# Revit family: Legrand Emergency Lighting_BAP-SPOTLIGHT
name_source: partatom
category: Luminaires
units: mm (PartAtom-declared; Revit-internal decimal feet)

## family parameters
Cote de connecteur circulaire = Utiliser le diamètre
Couper avec des vides une fois chargée = Non
Hôte = Face
Partagée = Non
Repere pour localisation dans la piece = Non
Source d'éclairage = Non
Type d'élément = Normal

## types (8) — shared parameters
Color = Black
Connected Object = Non
Connection type = other
ETIM Class = EC001957-Emergency luminaire
Elévation par défaut = 2300 mm
Emergency power supply = Autonomous (individual battery)
Fabricant = Legrand
Frequency = 50/60 Hz
Function = Escape and mood lighting
General Conditions of Use = https://export.legrand.com
Height = 94 mm
IK = 07
IP = 65
Installation method = Surface mounting (wall)
Material = Plastic
Operating temperature MIN-MAX = 0°C +35°C
Pictogram type = other
Power supply = 230 VAC
Protection class = II
Standby consumption = 0 A
Switching type = Non permanent
System power = 1 W
URL = https://www.legrand.fr
battery status = Lithium-ion
light source = LED not exchangeable
terminal capacity = 1,5-2,5 mm2

## per-type parameters (varying)
| type | 1 phare 1000lm | 2 phares 1500lm | 2 phares 2500lm | Autonomy | Control system | EAN Code | Large | Length | Long | Product Description | Reference | Spare battery | Useful luminous flux | Width |
| Spotlight Autotest 2500 lm 1H | Non | Non | Oui | 1 H | Autotest Automatic | 3414972656030 | 240 mm  [stored 0.787402 ft] | 286 mm | 286 mm | TWIN LEDS SPOTLIGHT EMERGENCY LIGHTING UNIT NON MAINTAINED 2500LM 1H AUTOTEST | 660463 | 2 x 660977 | 2500 lm | 240 mm  [stored 0.787402 ft] |
| Spotlight Autotest 1000 lm 1H | Oui | Non | Non | 1 H | Autotest Automatic | 3414972656016 | 137 mm  [stored 0.449475 ft] | 409 mm | 409 mm | SPOTLIGHT EMERGENCY LIGHTING UNIT NON MAINTAINED 1000LM 1H AUTOTEST | 660460 | 660976 | 1000 lm | 137 mm  [stored 0.449475 ft] |
| Spotlight Autotest 1500 lm 1H | Non | Oui | Non | 1 H | Autotest Automatic | 3414972656023 | 240 mm  [stored 0.787402 ft] | 286 mm | 286 mm | TWIN LEDS SPOTLIGHT EMERGENCY LIGHTING UNIT NON MAINTAINED 1500LM 1H AUTOTEST | 660462 | 1 x 660977 | 1500 lm | 240 mm  [stored 0.787402 ft] |
| Spotlight Autotest 1500 lm 2H | Non | Oui | Non | 2 H | Autotest Automatic | 3414972656047 | 240 mm  [stored 0.787402 ft] | 286 mm | 286 mm | TWIN LEDS SPOTLIGHT EMERGENCY LIGHTING UNIT NON MAINTAINED 1500LM 2H AUTOTEST | 660465 | 2 x 660977 | 1500 lm | 240 mm  [stored 0.787402 ft] |
| Spotlight Standard 1000 lm 1H | Oui | Non | Non | 1 H | Control key | 3414972656054 | 137 mm  [stored 0.449475 ft] | 409 mm | 409 mm | SPOTLIGHT EMERGENCY LIGHTING UNIT NON MAINTAINED 1000LM 1H STANDARD | 661460 | 660976 | 1000 lm | 137 mm  [stored 0.449475 ft] |
| Spotlight Standard 1500 lm 1H | Non | Oui | Non | 1 H | Control key | 3414972656061 | 240 mm  [stored 0.787402 ft] | 286 mm | 286 mm | TWIN LEDS SPOTLIGHT EMERGENCY LIGHTING UNIT NON MAINTAINED 1500LM 1H STANDARD | 661462 | 660977 | 1500 lm | 240 mm  [stored 0.787402 ft] |
| Spotlight Standard 2500 lm 1H | Non | Non | Oui | 1 H | Control key | 3414972656078 | 240 mm  [stored 0.787402 ft] | 286 mm | 286 mm | TWIN LEDS SPOTLIGHT EMERGENCY LIGHTING UNIT NON MAINTAINED 2500LM 1H STANDARD | 661463 | 2 x 660977 | 2500 lm | 240 mm  [stored 0.787402 ft] |
| Spotlight Adressable 2500 lm 1H | Non | Non | Oui | 1 H | Autotest Automatic | 3414972656085 | 240 mm  [stored 0.787402 ft] | 286 mm | 286 mm | TWIN LEDS SPOTLIGHT EMERGENCY LIGHTING UNIT NON MAINTAINED 2500LM 1H ADRESSABLE | 662463 | 2 x 660977 | 2500 lm | 240 mm  [stored 0.787402 ft] |

note: [stored X ft] marks values corroborated as IEEE doubles in the binary element streams (Revit-internal decimal feet)
